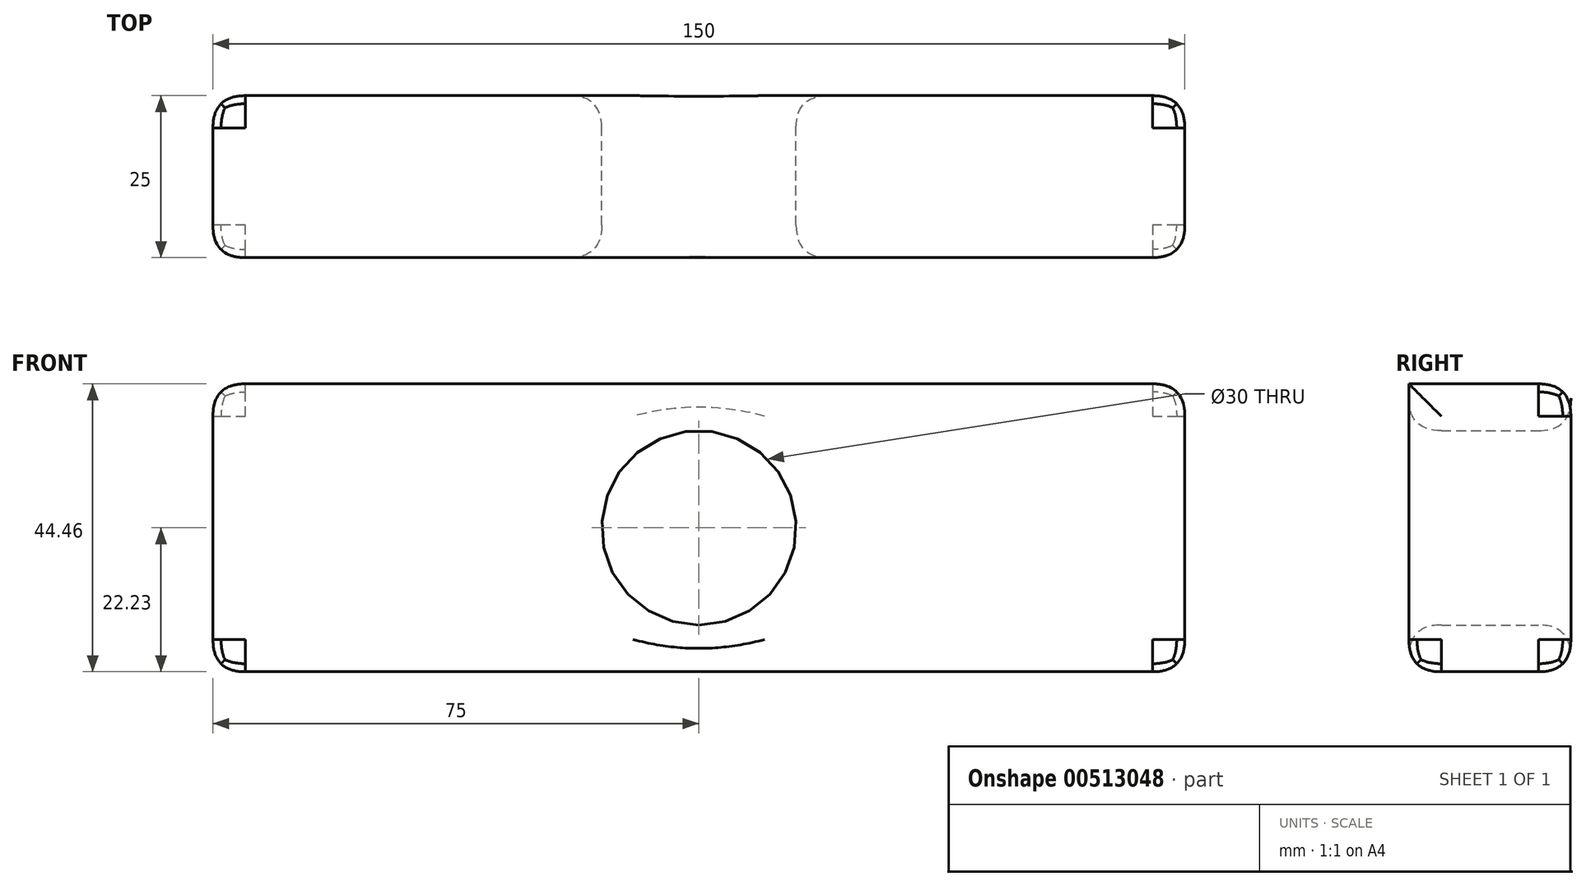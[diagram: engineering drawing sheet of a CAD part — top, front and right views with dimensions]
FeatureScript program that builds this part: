
annotation { "Feature Type Name" : "Feature", "Feature Type Description" : "" }
export const myFeature = defineFeature(function(context is Context, id is Id, definition is map)
    precondition{}
    {
        {
            var Q0;
            Q0=qCreatedBy(makeId("Front.planeOp"),FACE);
            var sketch = newSketch(context, id + "F0", { "sketchPlane" : qUnion([Q0])});
            skLineSegment(sketch, "E0.bottom", {"start": v(-75, 22.23) * mm, "end": v(75, 22.23) * mm});
            skLineSegment(sketch, "E0.top", {"start": v(-75, -22.23) * mm, "end": v(75, -22.23) * mm});
            skLineSegment(sketch, "E0.left", {"start": v(-75, 22.23) * mm, "end": v(-75, -22.23) * mm});
            skLineSegment(sketch, "E0.right", {"start": v(75, 22.23) * mm, "end": v(75, -22.23) * mm});
            skPoint(sketch, "E0.middle", {"position": v(0, 0) * mm});
            skCircle(sketch, "E1", {"center": v(0, 0) * mm, "radius": 15 * mm});
            skSolve(sketch);
        }
        {
            var Q0;
            Q0 = qSketchRegion(id + "F0", true);
            extrude(context, id + "F1", {"entities" : qUnion([Q0]), "depth" : 25 * mm});
        }
        {
            var Q0;
            Q0=makeQuery(id+"F1.opExtrude","CAP_EDGE",EDGE,{"disambiguationData":[OSD([sQuery(id+"F0.wireOp",EDGE,"E0.top")])],"isStart":true});
            var Q1;
            Q1=makeQuery(id+"F1.opExtrude","CAP_EDGE",EDGE,{"disambiguationData":[OSD([sQuery(id+"F0.wireOp",EDGE,"E0.top")])],"isStart":false});
            var Q2;
            Q2=makeQuery(id+"F1.opExtrude","CAP_EDGE",EDGE,{"disambiguationData":[OSD([sQuery(id+"F0.wireOp",EDGE,"E0.bottom")])],"isStart":true});
            var Q3;
            Q3=makeQuery(id+"F1.opExtrude","SWEPT_FACE",FACE,{"disambiguationData":[OSD([sQuery(id+"F0.wireOp",EDGE,"E0.left")])]});
            var Q4;
            Q4=makeQuery(id+"F1.opExtrude","SWEPT_FACE",FACE,{"disambiguationData":[OSD([sQuery(id+"F0.wireOp",EDGE,"E0.right")])]});
            var Q5;
            Q5=makeQuery(id+"F1.opExtrude","CAP_EDGE",EDGE,{"disambiguationData":[OSD([sQuery(id+"F0.wireOp",EDGE,"E1")])],"isStart":true});
            var Q6;
            Q6=makeQuery(id+"F1.opExtrude","SWEPT_FACE",FACE,{"disambiguationData":[OSD([sQuery(id+"F0.wireOp",EDGE,"E1")])]});
            fillet(context, id + "F2", {"entities" : qUnion([Q0, Q1, Q2, Q3, Q4, Q5, Q6]), "radius" : 5 * mm, "tangentPropagation" : true, "rho" : 0.5, "crossSection" : FilletCrossSection.CONIC, "allowEdgeOverflow" : false});
        }
    });
